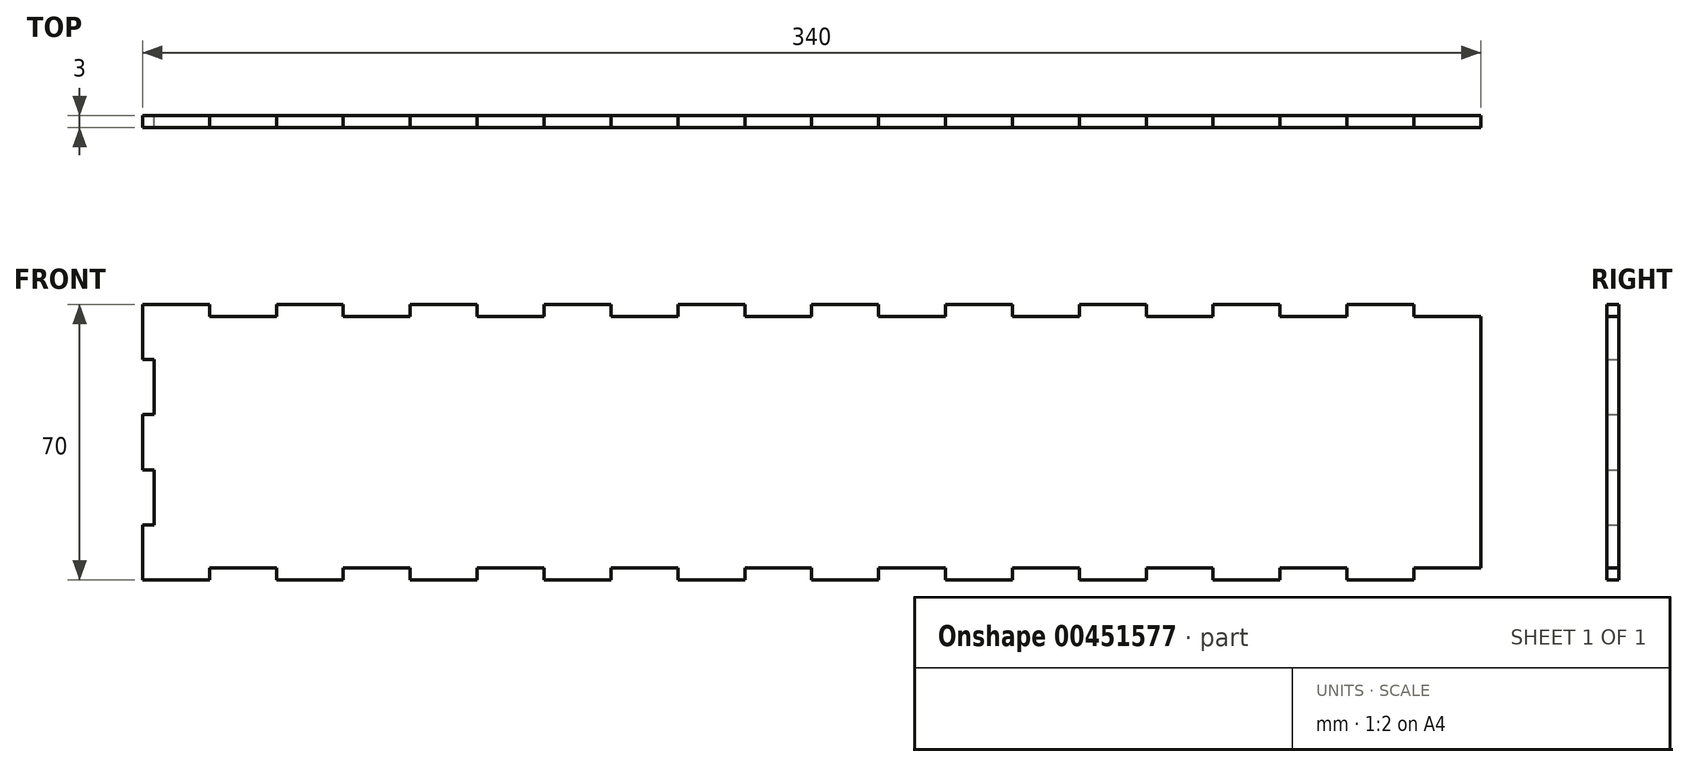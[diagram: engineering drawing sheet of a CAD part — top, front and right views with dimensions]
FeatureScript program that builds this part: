
annotation { "Feature Type Name" : "Feature", "Feature Type Description" : "" }
export const myFeature = defineFeature(function(context is Context, id is Id, definition is map)
    precondition{}
    {
        {
            var Q0;
            Q0=qCreatedBy(makeId("Front.planeOp"),FACE);
            var sketch = newSketch(context, id + "F0", { "sketchPlane" : qUnion([Q0])});
            skLineSegment(sketch, "E0.top", {"start": v(153, 35) * mm, "end": v(136, 35) * mm});
            skLineSegment(sketch, "E0.left", {"start": v(170, -32) * mm, "end": v(170, 32) * mm});
            skLineSegment(sketch, "E0.right", {"start": v(-170, -35) * mm, "end": v(-170, -21) * mm});
            skPoint(sketch, "E0.middle", {"position": v(0, 0) * mm});
            skLineSegment(sketch, "E1", {"start": v(-153, 32) * mm, "end": v(-136, 32) * mm});
            skLineSegment(sketch, "E2", {"start": v(-153, 35) * mm, "end": v(-153, 32) * mm});
            skLineSegment(sketch, "E3", {"start": v(-136, 35) * mm, "end": v(-136, 32) * mm});
            skLineSegment(sketch, "E4", {"start": v(-119, 35) * mm, "end": v(-119, 32) * mm});
            skLineSegment(sketch, "E5", {"start": v(-102, 35) * mm, "end": v(-102, 32) * mm});
            skLineSegment(sketch, "E6", {"start": v(-85, 35) * mm, "end": v(-85, 32) * mm});
            skLineSegment(sketch, "E7", {"start": v(-68, 35) * mm, "end": v(-68, 32) * mm});
            skLineSegment(sketch, "E8", {"start": v(-34, 35) * mm, "end": v(-34, 32) * mm});
            skLineSegment(sketch, "E9", {"start": v(-17, 35) * mm, "end": v(-17, 32) * mm});
            skLineSegment(sketch, "E10", {"start": v(-51, 35) * mm, "end": v(-51, 32) * mm});
            skLineSegment(sketch, "E11", {"start": v(0, 35) * mm, "end": v(0, 32) * mm});
            skLineSegment(sketch, "E12.MirrorCS", {"start": v(17, 35) * mm, "end": v(17, 32) * mm});
            skLineSegment(sketch, "E13.MirrorCS", {"start": v(51, 35) * mm, "end": v(51, 32) * mm});
            skLineSegment(sketch, "E14.MirrorCS", {"start": v(34, 35) * mm, "end": v(34, 32) * mm});
            skLineSegment(sketch, "E15.MirrorCS", {"start": v(68, 35) * mm, "end": v(68, 32) * mm});
            skLineSegment(sketch, "E16.MirrorCS", {"start": v(85, 35) * mm, "end": v(85, 32) * mm});
            skLineSegment(sketch, "E17.MirrorCS", {"start": v(102, 35) * mm, "end": v(102, 32) * mm});
            skLineSegment(sketch, "E18.MirrorCS", {"start": v(119, 35) * mm, "end": v(119, 32) * mm});
            skLineSegment(sketch, "E19.MirrorCS", {"start": v(136, 35) * mm, "end": v(136, 32) * mm});
            skLineSegment(sketch, "E20.MirrorCS", {"start": v(153, 35) * mm, "end": v(153, 32) * mm});
            skLineSegment(sketch, "E21.trimOffspring", {"start": v(-153, 35) * mm, "end": v(-170, 35) * mm});
            skLineSegment(sketch, "E22.trimOffspring", {"start": v(-119, 32) * mm, "end": v(-102, 32) * mm});
            skLineSegment(sketch, "E23.trimOffspring", {"start": v(-119, 35) * mm, "end": v(-136, 35) * mm});
            skLineSegment(sketch, "E24.trimOffspring", {"start": v(-85, 32) * mm, "end": v(-68, 32) * mm});
            skLineSegment(sketch, "E25.trimOffspring", {"start": v(-85, 35) * mm, "end": v(-102, 35) * mm});
            skLineSegment(sketch, "E26.trimOffspring", {"start": v(-51, 32) * mm, "end": v(-34, 32) * mm});
            skLineSegment(sketch, "E27.trimOffspring", {"start": v(-51, 35) * mm, "end": v(-68, 35) * mm});
            skLineSegment(sketch, "E28.trimOffspring", {"start": v(-17, 32) * mm, "end": v(0, 32) * mm});
            skLineSegment(sketch, "E29.trimOffspring", {"start": v(-17, 35) * mm, "end": v(-34, 35) * mm});
            skLineSegment(sketch, "E30.trimOffspring", {"start": v(17, 32) * mm, "end": v(34, 32) * mm});
            skLineSegment(sketch, "E31.trimOffspring", {"start": v(17, 35) * mm, "end": v(0, 35) * mm});
            skLineSegment(sketch, "E32.trimOffspring", {"start": v(51, 32) * mm, "end": v(68, 32) * mm});
            skLineSegment(sketch, "E33.trimOffspring", {"start": v(51, 35) * mm, "end": v(34, 35) * mm});
            skLineSegment(sketch, "E34.trimOffspring", {"start": v(85, 32) * mm, "end": v(102, 32) * mm});
            skLineSegment(sketch, "E35.trimOffspring", {"start": v(85, 35) * mm, "end": v(68, 35) * mm});
            skLineSegment(sketch, "E36.trimOffspring", {"start": v(119, 32) * mm, "end": v(136, 32) * mm});
            skLineSegment(sketch, "E37.trimOffspring", {"start": v(119, 35) * mm, "end": v(102, 35) * mm});
            skLineSegment(sketch, "E38.trimOffspring", {"start": v(153, 32) * mm, "end": v(170, 32) * mm});
            skLineSegment(sketch, "E39.MirrorCS", {"start": v(0, -35) * mm, "end": v(0, -32) * mm});
            skLineSegment(sketch, "E40.MirrorCS", {"start": v(85, -35) * mm, "end": v(85, -32) * mm});
            skLineSegment(sketch, "E41.MirrorCS", {"start": v(68, -35) * mm, "end": v(68, -32) * mm});
            skLineSegment(sketch, "E42.MirrorCS", {"start": v(34, -35) * mm, "end": v(34, -32) * mm});
            skLineSegment(sketch, "E43.MirrorCS", {"start": v(-51, -35) * mm, "end": v(-51, -32) * mm});
            skLineSegment(sketch, "E44.MirrorCS", {"start": v(-17, -35) * mm, "end": v(-17, -32) * mm});
            skLineSegment(sketch, "E45.MirrorCS", {"start": v(-34, -35) * mm, "end": v(-34, -32) * mm});
            skLineSegment(sketch, "E46.MirrorCS", {"start": v(-102, -35) * mm, "end": v(-102, -32) * mm});
            skLineSegment(sketch, "E47.MirrorCS", {"start": v(-136, -35) * mm, "end": v(-136, -32) * mm});
            skLineSegment(sketch, "E48.MirrorCS", {"start": v(-153, -35) * mm, "end": v(-153, -32) * mm});
            skLineSegment(sketch, "E49.MirrorCS", {"start": v(102, -35) * mm, "end": v(102, -32) * mm});
            skLineSegment(sketch, "E50.MirrorCS", {"start": v(17, -35) * mm, "end": v(17, -32) * mm});
            skLineSegment(sketch, "E51.MirrorCS", {"start": v(51, -35) * mm, "end": v(51, -32) * mm});
            skLineSegment(sketch, "E52.MirrorCS", {"start": v(136, -35) * mm, "end": v(136, -32) * mm});
            skLineSegment(sketch, "E53.MirrorCS", {"start": v(119, -35) * mm, "end": v(119, -32) * mm});
            skLineSegment(sketch, "E54.MirrorCS", {"start": v(-68, -35) * mm, "end": v(-68, -32) * mm});
            skLineSegment(sketch, "E55.MirrorCS", {"start": v(153, -35) * mm, "end": v(153, -32) * mm});
            skLineSegment(sketch, "E56.MirrorCS", {"start": v(-85, -35) * mm, "end": v(-85, -32) * mm});
            skLineSegment(sketch, "E57.MirrorCS", {"start": v(-119, -35) * mm, "end": v(-119, -32) * mm});
            skLineSegment(sketch, "E58.MirrorCS", {"start": v(-119, -35) * mm, "end": v(-136, -35) * mm});
            skLineSegment(sketch, "E59.MirrorCS", {"start": v(17, -35) * mm, "end": v(0, -35) * mm});
            skLineSegment(sketch, "E60.MirrorCS", {"start": v(85, -35) * mm, "end": v(68, -35) * mm});
            skLineSegment(sketch, "E61.MirrorCS", {"start": v(-17, -32) * mm, "end": v(0, -32) * mm});
            skLineSegment(sketch, "E62.MirrorCS", {"start": v(17, -32) * mm, "end": v(34, -32) * mm});
            skLineSegment(sketch, "E63.MirrorCS", {"start": v(51, -35) * mm, "end": v(34, -35) * mm});
            skLineSegment(sketch, "E64.MirrorCS", {"start": v(-51, -32) * mm, "end": v(-34, -32) * mm});
            skLineSegment(sketch, "E65.MirrorCS", {"start": v(119, -32) * mm, "end": v(136, -32) * mm});
            skLineSegment(sketch, "E66.MirrorCS", {"start": v(-85, -32) * mm, "end": v(-68, -32) * mm});
            skLineSegment(sketch, "E67.MirrorCS", {"start": v(153, -32) * mm, "end": v(170, -32) * mm});
            skLineSegment(sketch, "E68.MirrorCS", {"start": v(-85, -35) * mm, "end": v(-102, -35) * mm});
            skLineSegment(sketch, "E69.MirrorCS", {"start": v(119, -35) * mm, "end": v(102, -35) * mm});
            skLineSegment(sketch, "E70.MirrorCS", {"start": v(-153, -35) * mm, "end": v(-170, -35) * mm});
            skLineSegment(sketch, "E71.MirrorCS", {"start": v(153, -35) * mm, "end": v(136, -35) * mm});
            skLineSegment(sketch, "E72.MirrorCS", {"start": v(-119, -32) * mm, "end": v(-102, -32) * mm});
            skLineSegment(sketch, "E73.MirrorCS", {"start": v(85, -32) * mm, "end": v(102, -32) * mm});
            skLineSegment(sketch, "E74.MirrorCS", {"start": v(-17, -35) * mm, "end": v(-34, -35) * mm});
            skLineSegment(sketch, "E75.MirrorCS", {"start": v(-51, -35) * mm, "end": v(-68, -35) * mm});
            skLineSegment(sketch, "E76.MirrorCS", {"start": v(-153, -32) * mm, "end": v(-136, -32) * mm});
            skLineSegment(sketch, "E77.MirrorCS", {"start": v(51, -32) * mm, "end": v(68, -32) * mm});
            skLineSegment(sketch, "E78", {"start": v(-167, 21) * mm, "end": v(-167, 7) * mm});
            skLineSegment(sketch, "E79", {"start": v(-170, 21) * mm, "end": v(-167, 21) * mm});
            skLineSegment(sketch, "E80", {"start": v(-170, 7) * mm, "end": v(-167, 7) * mm});
            skLineSegment(sketch, "E81", {"start": v(-170, -7) * mm, "end": v(-167, -7) * mm});
            skLineSegment(sketch, "E82", {"start": v(-170, -21) * mm, "end": v(-167, -21) * mm});
            skLineSegment(sketch, "E83.trimOffspring", {"start": v(-170, 21) * mm, "end": v(-170, 35) * mm});
            skLineSegment(sketch, "E84.trimOffspring", {"start": v(-167, -7) * mm, "end": v(-167, -21) * mm});
            skLineSegment(sketch, "E85.trimOffspring", {"start": v(-170, -7) * mm, "end": v(-170, 7) * mm});
            skSolve(sketch);
        }
        {
            var Q0;
            Q0=makeQuery(id+"F0.imprint","IMPRINT",FACE,{"disambiguationData":[TD([[makeQuery(id+"F0.imprint","IMPRINT",EDGE,{"derivedFrom":sQuery(id+"F0.wireOp",EDGE,"E0.top")}),1.0]])]});
            extrude(context, id + "F1", {"entities" : qUnion([Q0]), "depth" : 3 * mm, "offsetDistance" : 25 * mm});
        }
    });
